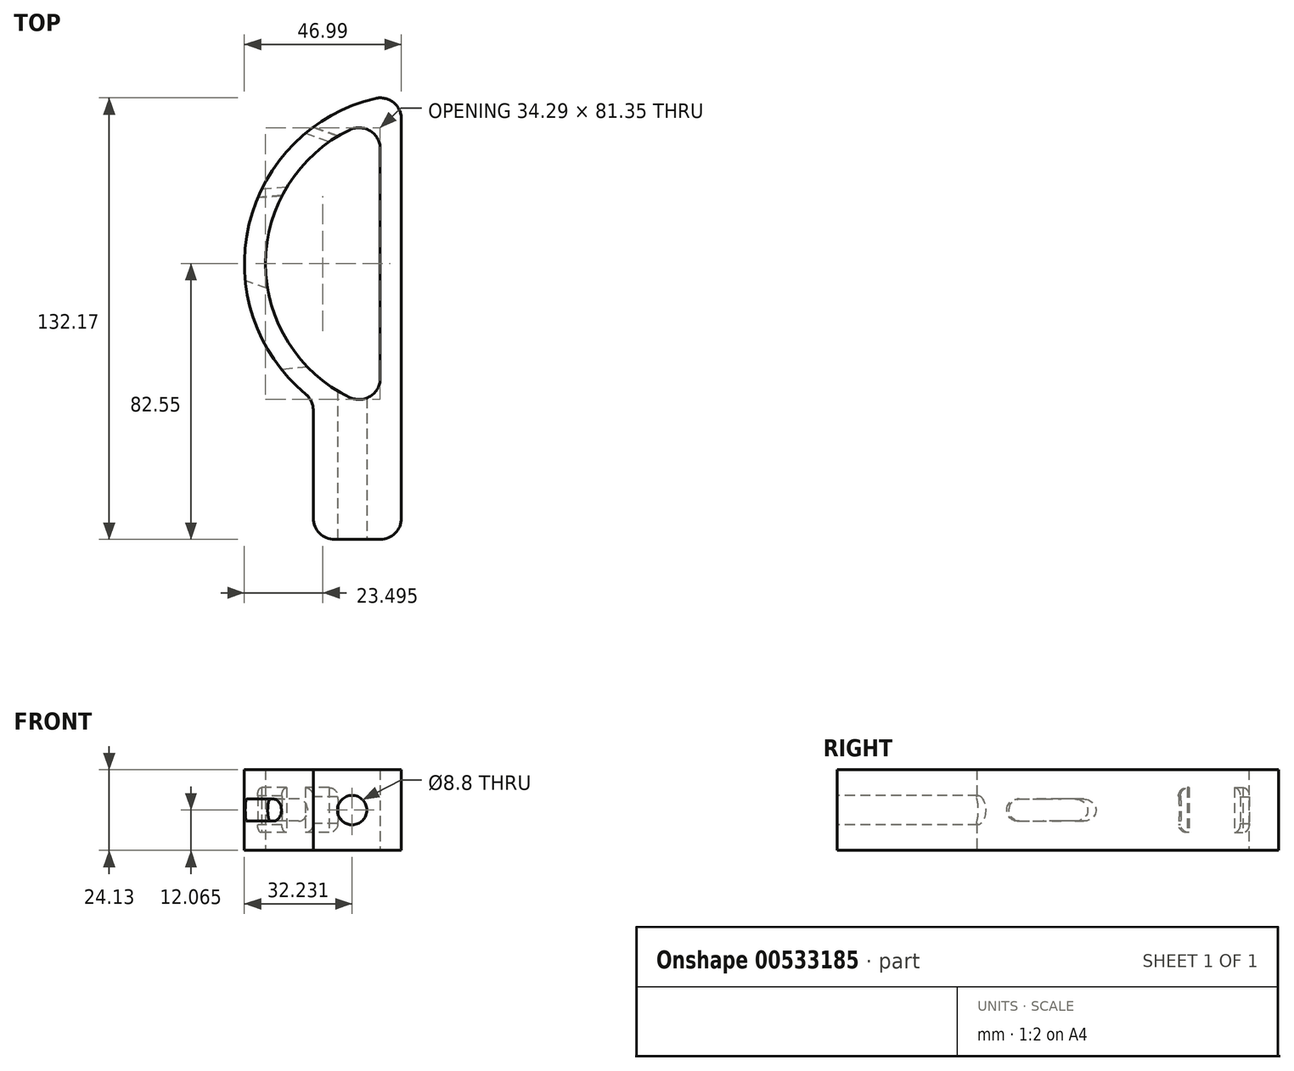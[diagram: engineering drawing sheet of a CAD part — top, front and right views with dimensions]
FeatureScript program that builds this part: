
annotation { "Feature Type Name" : "Feature", "Feature Type Description" : "" }
export const myFeature = defineFeature(function(context is Context, id is Id, definition is map)
    precondition{}
    {
        {
            var Q0;
            Q0=qCreatedBy(makeId("Top.planeOp"),FACE);
            var sketch = newSketch(context, id + "F0", { "sketchPlane" : qUnion([Q0])});
            skArc(sketch, "E0", {"start": v(-11.61, 49.46) * mm, "mid": v(-49.45, 11.65) * mm, "end": v(-32.47, -39.06) * mm});
            skArc(sketch, "E1", {"start": v(-19.26, 40.06) * mm, "mid": v(-44.45, 0) * mm, "end": v(-19.26, -40.06) * mm});
            skLineSegment(sketch, "E2", {"start": v(6.35, 44.45) * mm, "end": v(6.35, -50.8) * mm, "construction": true});
            skLineSegment(sketch, "E3", {"start": v(0, 37.57) * mm, "end": v(0, -37.57) * mm, "construction": true});
            skPoint(sketch, "E4", {"position": v(-50.8, 0) * mm});
            skPoint(sketch, "E5", {"position": v(-44.25, -24.96) * mm});
            skPoint(sketch, "E6", {"position": v(-47.9, 16.9) * mm});
            skPoint(sketch, "E7.visualSharp", {"position": v(6.35, 0) * mm});
            skPoint(sketch, "E8.visualSharp", {"position": v(0, 44.45) * mm});
            skPoint(sketch, "E9", {"position": v(-50.65, -3.9) * mm});
            skPoint(sketch, "E10", {"position": v(-36.28, 35.56) * mm});
            skLineSegment(sketch, "E11", {"start": v(0, 50.8) * mm, "end": v(0, 50.8) * mm});
            skLineSegment(sketch, "E12", {"start": v(-30.18, -43.95) * mm, "end": v(-30.18, -50.8) * mm});
            skLineSegment(sketch, "E13", {"start": v(-23.83, -82.55) * mm, "end": v(-10.16, -82.55) * mm});
            skPoint(sketch, "E14", {"position": v(-30.23, -32.59) * mm});
            skPoint(sketch, "E15.visualSharp", {"position": v(6.35, 50.8) * mm});
            skPoint(sketch, "E16.visualSharp", {"position": v(6.35, -82.55) * mm});
            skPoint(sketch, "E17.visualSharp", {"position": v(0, -44.45) * mm});
            skPoint(sketch, "E18.visualSharp", {"position": v(-30.18, -82.55) * mm});
            skLineSegment(sketch, "E19", {"start": v(-10.16, 34.34) * mm, "end": v(-10.16, -34.34) * mm});
            skLineSegment(sketch, "E20", {"start": v(-3.81, 43.27) * mm, "end": v(-3.8, -50.8) * mm});
            skPoint(sketch, "E21.visualSharp", {"position": v(-10.16, 43.27) * mm});
            skArc(sketch, "E21.filletArc", {"start": v(-10.16, 34.34) * mm, "mid": v(-13.13, 39.71) * mm, "end": v(-19.26, 40.06) * mm});
            skPoint(sketch, "E22.visualSharp", {"position": v(-3.81, 50.66) * mm});
            skArc(sketch, "E22.filletArc", {"start": v(-3.81, 43.27) * mm, "mid": v(-6.22, 48.25) * mm, "end": v(-11.61, 49.46) * mm});
            skPoint(sketch, "E23.visualSharp", {"position": v(-3.8, -82.55) * mm});
            skPoint(sketch, "E24.visualSharp", {"position": v(-10.16, -43.27) * mm});
            skArc(sketch, "E24.filletArc", {"start": v(-19.26, -40.06) * mm, "mid": v(-13.13, -39.71) * mm, "end": v(-10.16, -34.34) * mm});
            skLineSegment(sketch, "E25.top", {"start": v(-23.83, -82.55) * mm, "end": v(-23.83, -82.55) * mm});
            skLineSegment(sketch, "E25.left", {"start": v(-30.18, -50.8) * mm, "end": v(-30.18, -76.2) * mm});
            skLineSegment(sketch, "E26.top", {"start": v(-10.16, -82.55) * mm, "end": v(-10.16, -82.55) * mm});
            skLineSegment(sketch, "E26.left", {"start": v(-3.8, -50.8) * mm, "end": v(-3.8, -76.2) * mm});
            skArc(sketch, "E27.filletArc", {"start": v(-30.18, -76.2) * mm, "mid": v(-28.32, -80.7) * mm, "end": v(-23.83, -82.55) * mm});
            skArc(sketch, "E28.filletArc", {"start": v(-10.16, -82.55) * mm, "mid": v(-5.67, -80.7) * mm, "end": v(-3.8, -76.2) * mm});
            skPoint(sketch, "E29.visualSharp", {"position": v(-30.18, -40.86) * mm});
            skArc(sketch, "E29.filletArc", {"start": v(-30.18, -43.95) * mm, "mid": v(-30.78, -41.25) * mm, "end": v(-32.47, -39.06) * mm});
            skSolve(sketch);
        }
        {
            var Q0;
            Q0=makeQuery(id+"F0.imprint","IMPRINT",FACE,{"disambiguationData":[TD([[makeQuery(id+"F0.imprint","IMPRINT",EDGE,{"derivedFrom":sQuery(id+"F0.wireOp",EDGE,"E0")}),1.0]])]});
            extrude(context, id + "F1", {"entities" : qUnion([Q0]), "depth" : 21.59 * mm, "offsetDistance" : 25.4 * mm, "hasSecondDirection" : true, "secondDirectionOppositeDirection" : true, "secondDirectionDepth" : 2.54 * mm});
        }
        {
            var Q0;
            Q0=makeQuery(id+"F1.opExtrude","SWEPT_FACE",FACE,{"disambiguationData":[OSD([sQuery(id+"F0.wireOp",EDGE,"E19")])]});
            cPlane(context, id + "F2", {"entities" : qUnion([Q0]), "cplaneType" : CPlaneType.OFFSET, "offset" : 40.64 * mm, "width" : 152.4 * mm, "height" : 152.4 * mm});
        }
        {
            var Q0;
            Q0=makeQuery(id+"F1.opExtrude","SWEPT_FACE",FACE,{"disambiguationData":[OSD([sQuery(id+"F0.wireOp",EDGE,"E13")])]});
            var sketch = newSketch(context, id + "F3", { "sketchPlane" : qUnion([Q0])});
            skPoint(sketch, "E30", {"position": v(-18.57, 9.53) * mm});
            skSolve(sketch);
        }
        {
            var Q0;
            Q0=sQuery(id+"F3.wireOp",VERTEX,"E30");
            var Q1;
            Q1=makeQuery(id+"F1.opExtrude","SWEPT_BODY",BODY,{"disambiguationData":[OSD([sQuery(id+"F0.wireOp",EDGE,"E0"),sQuery(id+"F0.wireOp",EDGE,"E1"),sQuery(id+"F0.wireOp",EDGE,"EP9hLKmM-xL3O-Gp7G-3c1h-ResquHTWNDlz"),sQuery(id+"F0.wireOp",EDGE,"E2"),sQuery(id+"F0.wireOp",EDGE,"dOx9RUUg-dijC-ZvtV-rfcF-Oi3RTDK4aGwI"),sQuery(id+"F0.wireOp",EDGE,"E3"),sQuery(id+"F0.wireOp",EDGE,"hJY3wXVF-1q9m-Ns05-G3qi-C3trqGpT6wyA"),sQuery(id+"F0.wireOp",EDGE,"3lB0U4jL-FZEo-ribd-zVyk-iThvpHzQjLYy")])]});
            hole(context, id + "F4", {"style" : HoleStyle.SIMPLE, "endStyle" : HoleEndStyle.BLIND, "standardTappedOrClearance" : lookupTablePath({ "standard" : "ISO", "fit" : "Normal", "size" : "M8", "type" : "Clearance" }), "standardBlindInLast" : lookupTablePath({ "fit" : "Standard", "standard" : "ISO", "size" : "M8", "type" : "Clearance" }), "holeDiameter" : 8.8 * mm, "holeDepth" : 50.8 * mm, "isTappedThrough" : true, "tappedDepth" : 12.7 * mm, "tapClearance" : 3, "locations" : qUnion([Q0]), "scope" : qUnion([Q1]), "majorDiameter" : 10 * mm});
        }
        {
            var Q0;
            Q0=qCreatedBy(id+"F2.planeOp",FACE);
            var sketch = newSketch(context, id + "F5", { "sketchPlane" : qUnion([Q0])});
            skPoint(sketch, "E31", {"position": v(-17.21, 0) * mm});
            skPoint(sketch, "E32", {"position": v(-35.87, 0) * mm});
            skPoint(sketch, "E33", {"position": v(3.6, 0) * mm});
            skPoint(sketch, "E34", {"position": v(24.65, 0) * mm});
            skLineSegment(sketch, "E35", {"start": v(-35.87, 0) * mm, "end": v(-35.87, 19.05) * mm});
            skLineSegment(sketch, "E36", {"start": v(-17.21, 0) * mm, "end": v(-17.21, 19.05) * mm});
            skLineSegment(sketch, "E37", {"start": v(3.6, 0) * mm, "end": v(3.6, 7.02) * mm});
            skLineSegment(sketch, "E38", {"start": v(24.65, 0) * mm, "end": v(24.65, 7.02) * mm});
            skArc(sketch, "E39", {"start": v(-35.87, 16.26) * mm, "mid": v(-37.56, 15.6) * mm, "end": v(-38.36, 13.97) * mm});
            skArc(sketch, "E40.MirrorCS", {"start": v(-35.87, 2.8) * mm, "mid": v(-37.56, 3.45) * mm, "end": v(-38.36, 5.08) * mm});
            skArc(sketch, "E41", {"start": v(-38.36, 13.97) * mm, "mid": v(-38.54, 9.52) * mm, "end": v(-38.36, 5.08) * mm});
            skLineSegment(sketch, "E42", {"start": v(-35.87, 5.3) * mm, "end": v(-35.87, 13.76) * mm});
            skPoint(sketch, "E43", {"position": v(-35.87, 9.52) * mm});
            skLineSegment(sketch, "E44", {"start": v(-1.84, -3.07) * mm, "end": v(-1.84, 15.98) * mm});
            skArc(sketch, "E45", {"start": v(-14.72, 13.55) * mm, "mid": v(-15.37, 15.45) * mm, "end": v(-17.21, 16.26) * mm});
            skArc(sketch, "E46.MirrorCS", {"start": v(-14.72, 5.5) * mm, "mid": v(-15.37, 3.6) * mm, "end": v(-17.21, 2.8) * mm});
            skArc(sketch, "E47", {"start": v(-14.72, 13.55) * mm, "mid": v(-14.89, 9.52) * mm, "end": v(-14.72, 5.5) * mm});
            skLineSegment(sketch, "E48", {"start": v(-17.21, 5.3) * mm, "end": v(-17.21, 13.76) * mm});
            skPoint(sketch, "E49", {"position": v(-17.21, 9.53) * mm});
            skLineSegment(sketch, "E50", {"start": v(-35.87, 2.8) * mm, "end": v(-17.21, 2.8) * mm});
            skLineSegment(sketch, "E51", {"start": v(-35.87, 16.26) * mm, "end": v(-17.21, 16.26) * mm});
            skArc(sketch, "E52", {"start": v(3.6, 12.03) * mm, "mid": v(1.1, 9.52) * mm, "end": v(3.6, 7.02) * mm});
            skArc(sketch, "E53", {"start": v(24.65, 7.02) * mm, "mid": v(27.15, 9.52) * mm, "end": v(24.65, 12.03) * mm});
            skLineSegment(sketch, "E54", {"start": v(3.6, 12.03) * mm, "end": v(24.65, 12.03) * mm});
            skLineSegment(sketch, "E55", {"start": v(3.6, 7.02) * mm, "end": v(24.65, 7.02) * mm});
            skLineSegment(sketch, "E56.trimOffspring", {"start": v(3.6, 12.03) * mm, "end": v(3.6, 19.05) * mm});
            skLineSegment(sketch, "E57.trimOffspring", {"start": v(24.65, 12.03) * mm, "end": v(24.65, 19.05) * mm});
            skSolve(sketch);
        }
        {
            var Q0;
            Q0=sQuery(id+"F5.wireOp",EDGE,"E44");
            cPlane(context, id + "F6", {"entities" : qUnion([Q0]), "cplaneType" : CPlaneType.LINE_ANGLE, "offset" : 25.4 * mm, "angle" : 20 * degree, "oppositeDirection" : true, "width" : 152.4 * mm, "height" : 152.4 * mm});
        }
        {
            var Q0;
            Q0=qCreatedBy(id+"F6.planeOp",FACE);
            cPlane(context, id + "F7", {"entities" : qUnion([Q0]), "cplaneType" : CPlaneType.OFFSET, "offset" : 12.7 * mm, "oppositeDirection" : true, "width" : 152.4 * mm, "height" : 152.4 * mm});
        }
        {
            var Q0;
            Q0=qCreatedBy(id+"F7.planeOp",FACE);
            var sketch = newSketch(context, id + "F8", { "sketchPlane" : qUnion([Q0])});
            skPoint(sketch, "E58", {"position": v(25.47, 0) * mm});
            skLineSegment(sketch, "E59", {"start": v(13.01, 2.8) * mm, "end": v(13.01, 16.26) * mm});
            skLineSegment(sketch, "E60", {"start": v(25.47, 0) * mm, "end": v(25.47, 19.05) * mm});
            skLineSegment(sketch, "E61", {"start": v(13.01, 5.3) * mm, "end": v(13.01, 13.76) * mm});
            skPoint(sketch, "E62", {"position": v(13.01, 9.53) * mm});
            skArc(sketch, "E63", {"start": v(27.97, 13.55) * mm, "mid": v(27.31, 15.45) * mm, "end": v(25.47, 16.26) * mm});
            skArc(sketch, "E64.MirrorCS", {"start": v(27.97, 5.5) * mm, "mid": v(27.31, 3.6) * mm, "end": v(25.47, 2.8) * mm});
            skLineSegment(sketch, "E65", {"start": v(25.47, 5.3) * mm, "end": v(25.47, 13.76) * mm});
            skPoint(sketch, "E66", {"position": v(25.47, 9.53) * mm});
            skLineSegment(sketch, "E67", {"start": v(13.01, 2.8) * mm, "end": v(25.47, 2.8) * mm});
            skLineSegment(sketch, "E68", {"start": v(13.01, 16.26) * mm, "end": v(25.47, 16.26) * mm});
            skArc(sketch, "E69", {"start": v(27.97, 5.5) * mm, "mid": v(28.12, 9.53) * mm, "end": v(27.97, 13.55) * mm});
            skSolve(sketch);
        }
        {
            var Q0;
            Q0=sQuery(id+"F5.wireOp",EDGE,"E44");
            cPlane(context, id + "F9", {"entities" : qUnion([Q0]), "cplaneType" : CPlaneType.LINE_ANGLE, "offset" : 25.4 * mm, "angle" : 4.42 * degree, "width" : 152.4 * mm, "height" : 152.4 * mm});
        }
        {
            var Q0;
            Q0=qCreatedBy(id+"F9.planeOp",FACE);
            cPlane(context, id + "F10", {"entities" : qUnion([Q0]), "cplaneType" : CPlaneType.OFFSET, "offset" : 15.24 * mm, "oppositeDirection" : true, "width" : 152.4 * mm, "height" : 152.4 * mm});
        }
        {
            var Q0;
            Q0=qCreatedBy(id+"F10.planeOp",FACE);
            var sketch = newSketch(context, id + "F11", { "sketchPlane" : qUnion([Q0])});
            skPoint(sketch, "E70", {"position": v(33.33, 0) * mm});
            skPoint(sketch, "E71", {"position": v(25.7, 0) * mm});
            skLineSegment(sketch, "E72", {"start": v(25.7, 0) * mm, "end": v(25.7, 19.05) * mm});
            skLineSegment(sketch, "E73", {"start": v(33.33, 0) * mm, "end": v(33.33, 19.05) * mm});
            skArc(sketch, "E74", {"start": v(25.7, 16.26) * mm, "mid": v(23.93, 15.52) * mm, "end": v(23.2, 13.73) * mm});
            skArc(sketch, "E75.MirrorCS", {"start": v(25.7, 2.8) * mm, "mid": v(24.02, 3.45) * mm, "end": v(23.22, 5.08) * mm});
            skLineSegment(sketch, "E76", {"start": v(25.7, 5.3) * mm, "end": v(25.7, 13.76) * mm});
            skPoint(sketch, "E77", {"position": v(25.7, 9.52) * mm});
            skArc(sketch, "E78", {"start": v(35.82, 13.55) * mm, "mid": v(35.17, 15.45) * mm, "end": v(33.33, 16.26) * mm});
            skArc(sketch, "E79.MirrorCS", {"start": v(35.82, 5.5) * mm, "mid": v(35.17, 3.6) * mm, "end": v(33.33, 2.8) * mm});
            skArc(sketch, "E80", {"start": v(35.82, 13.55) * mm, "mid": v(35.65, 9.52) * mm, "end": v(35.82, 5.5) * mm});
            skLineSegment(sketch, "E81", {"start": v(33.33, 5.3) * mm, "end": v(33.33, 13.76) * mm});
            skPoint(sketch, "E82", {"position": v(33.33, 9.52) * mm});
            skLineSegment(sketch, "E83", {"start": v(25.7, 2.8) * mm, "end": v(33.33, 2.8) * mm});
            skLineSegment(sketch, "E84", {"start": v(25.7, 16.26) * mm, "end": v(33.33, 16.26) * mm});
            skArc(sketch, "E85", {"start": v(23.22, 5.08) * mm, "mid": v(23.4, 9.4) * mm, "end": v(23.2, 13.73) * mm});
            skSolve(sketch);
        }
        {
            var Q0;
            {var subQ1=sQuery(id+"F8.wireOp",EDGE,"E63");Q0=makeQuery(id+"F8.imprint","IMPRINT",FACE,{"disambiguationData":[TD([[makeQuery(id+"F8.imprint","IMPRINT",EDGE,{"derivedFrom":subQ1}),1.0]])]});}
            var Q1;
            {var subQ5=sQuery(id+"F8.wireOp",EDGE,"E61");Q1=makeQuery(id+"F8.imprint","IMPRINT",FACE,{"disambiguationData":[TD([[makeQuery(id+"F8.imprint","IMPRINT",EDGE,{"derivedFrom":subQ5}),-1.0]])]});}
            var Q2;
            {var subQ0=sQuery(id+"F8.wireOp",EDGE,"79d6455e-a1dc-483f-a46f-3cff99740c98");Q2=makeQuery(id+"F8.imprint","IMPRINT",FACE,{"disambiguationData":[TD([[makeQuery(id+"F8.imprint","IMPRINT",EDGE,{"derivedFrom":subQ0}),1.0]])]});}
            extrude(context, id + "F12", {"entities" : qUnion([Q0, Q1, Q2]), "operationType" : NewBodyOperationType.REMOVE, "depth" : 38.1 * mm, "offsetDistance" : 25.4 * mm});
        }
        {
            var Q0;
            {var subQ5=sQuery(id+"F11.wireOp",EDGE,"E76");Q0=makeQuery(id+"F11.imprint","IMPRINT",FACE,{"disambiguationData":[TD([[makeQuery(id+"F11.imprint","IMPRINT",EDGE,{"derivedFrom":subQ5}),-1.0]])]});}
            var Q1;
            {var subQ0=sQuery(id+"F11.wireOp",EDGE,"E74");Q1=makeQuery(id+"F11.imprint","IMPRINT",FACE,{"disambiguationData":[TD([[makeQuery(id+"F11.imprint","IMPRINT",EDGE,{"derivedFrom":subQ0}),1.0]])]});}
            extrude(context, id + "F13", {"entities" : qUnion([Q0, Q1]), "operationType" : NewBodyOperationType.REMOVE, "depth" : 44.45 * mm, "offsetDistance" : 25.4 * mm});
        }
        {
            var Q0;
            Q0=sQuery(id+"F5.wireOp",EDGE,"E44");
            cPlane(context, id + "F14", {"entities" : qUnion([Q0]), "cplaneType" : CPlaneType.LINE_ANGLE, "offset" : 25.4 * mm, "angle" : 20 * degree, "oppositeDirection" : true, "width" : 152.4 * mm, "height" : 152.4 * mm});
        }
        {
            var Q0;
            Q0=qCreatedBy(id+"F14.planeOp",FACE);
            var sketch = newSketch(context, id + "F15", { "sketchPlane" : qUnion([Q0])});
            skArc(sketch, "E86", {"start": v(-25.33, 6.22) * mm, "mid": v(-22.02, 9.52) * mm, "end": v(-25.33, 12.83) * mm});
            skLineSegment(sketch, "E87", {"start": v(-35.49, 12.83) * mm, "end": v(-25.33, 12.83) * mm});
            skLineSegment(sketch, "E88", {"start": v(-35.49, 6.22) * mm, "end": v(-25.33, 6.22) * mm});
            skLineSegment(sketch, "E89", {"start": v(-35.49, 6.22) * mm, "end": v(-35.49, 12.83) * mm});
            skSolve(sketch);
        }
        {
            var Q0;
            Q0=sQuery(id+"F5.wireOp",EDGE,"E44");
            cPlane(context, id + "F16", {"entities" : qUnion([Q0]), "cplaneType" : CPlaneType.LINE_ANGLE, "offset" : 25.4 * mm, "angle" : 5 * degree, "width" : 152.4 * mm, "height" : 152.4 * mm});
        }
        {
            var Q0;
            Q0=qCreatedBy(id+"F16.planeOp",FACE);
            cPlane(context, id + "F17", {"entities" : qUnion([Q0]), "cplaneType" : CPlaneType.OFFSET, "offset" : 38.1 * mm, "oppositeDirection" : true, "width" : 152.4 * mm, "height" : 152.4 * mm});
        }
        {
            var Q0;
            Q0=qCreatedBy(id+"F17.planeOp",FACE);
            var sketch = newSketch(context, id + "F18", { "sketchPlane" : qUnion([Q0])});
            skLineSegment(sketch, "E90.bottom", {"start": v(-11.74, 6.23) * mm, "end": v(-24.83, 6.23) * mm});
            skLineSegment(sketch, "E90.top", {"start": v(-11.74, 12.83) * mm, "end": v(-24.83, 12.83) * mm});
            skArc(sketch, "E91", {"start": v(-24.83, 12.83) * mm, "mid": v(-28.13, 9.53) * mm, "end": v(-24.83, 6.23) * mm});
            skLineSegment(sketch, "E92", {"start": v(-11.74, 12.83) * mm, "end": v(-11.74, 6.23) * mm});
            skSolve(sketch);
        }
        {
            var Q0;
            Q0=makeQuery(id+"F18.imprint","IMPRINT",FACE,{"disambiguationData":[TD([[makeQuery(id+"F18.imprint","IMPRINT",EDGE,{"derivedFrom":sQuery(id+"F18.wireOp",EDGE,"E90.bottom")}),-1.0]])]});
            var Q1;
            Q1=makeQuery(id+"F1.opExtrude","SWEPT_FACE",FACE,{"disambiguationData":[OSD([sQuery(id+"F0.wireOp",EDGE,"E3")])]});
            extrude(context, id + "F19", {"entities" : qUnion([Q0]), "operationType" : NewBodyOperationType.REMOVE, "depth" : 73.66 * mm, "endBoundEntityFace" : qUnion([Q1]), "offsetDistance" : 25.4 * mm});
        }
        {
            var Q0;
            Q0 = qSketchRegion(id + "F15", true);
            extrude(context, id + "F20", {"entities" : qUnion([Q0]), "operationType" : NewBodyOperationType.REMOVE, "depth" : 20.32 * mm, "offsetDistance" : 25.4 * mm});
        }
    });
